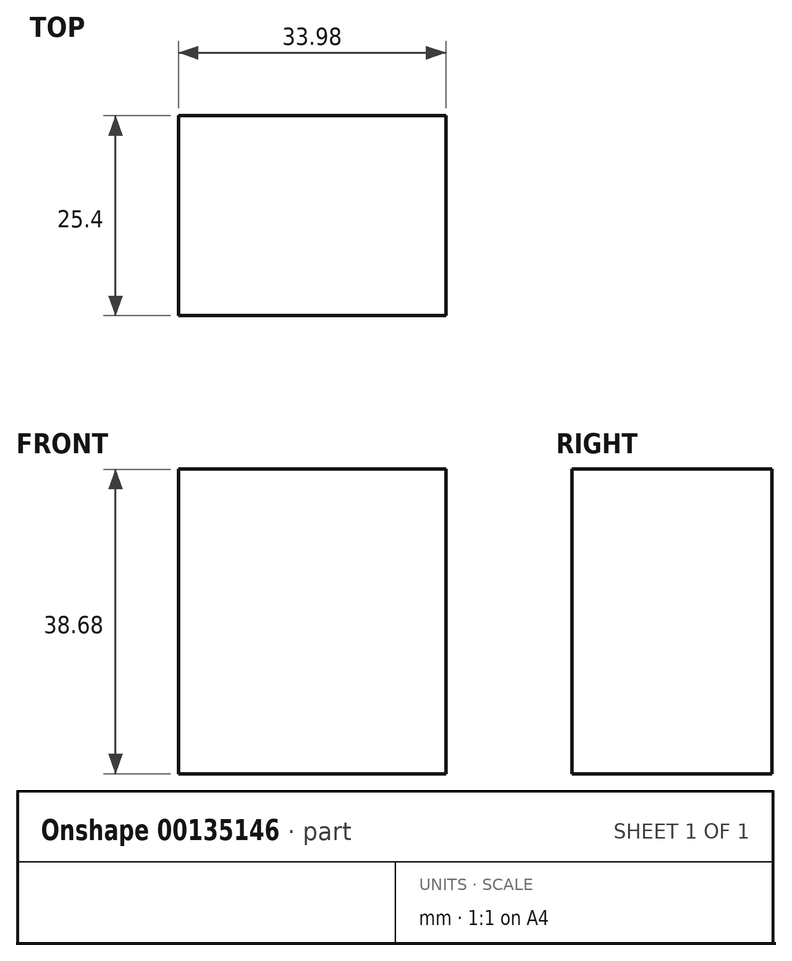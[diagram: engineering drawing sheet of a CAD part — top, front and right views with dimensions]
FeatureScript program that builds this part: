
annotation { "Feature Type Name" : "Feature", "Feature Type Description" : "" }
export const myFeature = defineFeature(function(context is Context, id is Id, definition is map)
    precondition{}
    {
        {
            var Q0;
            Q0=qCreatedBy(makeId("Front.planeOp"),FACE);
            var sketch = newSketch(context, id + "F0", { "sketchPlane" : qUnion([Q0])});
            skLineSegment(sketch, "E0.bottom", {"start": v(0, 0) * mm, "end": v(33.98, 0) * mm});
            skLineSegment(sketch, "E0.top", {"start": v(0, 38.68) * mm, "end": v(33.98, 38.68) * mm});
            skLineSegment(sketch, "E0.left", {"start": v(0, 0) * mm, "end": v(0, 38.68) * mm});
            skLineSegment(sketch, "E0.right", {"start": v(33.98, 0) * mm, "end": v(33.98, 38.68) * mm});
            skSolve(sketch);
        }
        {
            var Q0;
            Q0=makeQuery(id+"F0.imprint","IMPRINT",FACE,{"disambiguationData":[TD([[makeQuery(id+"F0.imprint","IMPRINT",EDGE,{"derivedFrom":sQuery(id+"F0.wireOp",EDGE,"E0.bottom")}),1.0]])]});
            extrude(context, id + "F1", {"entities" : qUnion([Q0]), "depth" : 25.4 * mm});
        }
    });
